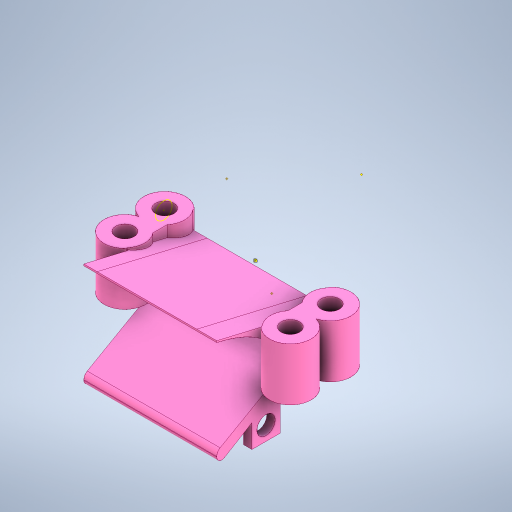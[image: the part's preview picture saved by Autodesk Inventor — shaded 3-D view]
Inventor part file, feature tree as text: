
AUTODESK INVENTOR PART (.ipt)
format: ipt  version: 2024 (Build 280153000, 153)  size: 1,867,264 bytes
history: native  units: mm
features: sketch x24, extrude x19, projected_geometry x11, split x10, other x10, loft x6, boolean_combine x5, plane x4, fillet x2, sweep x2, thicken_offset x2
ambient origin geometry x8: Origin, YZ Plane, XZ Plane, XY Plane, X Axis, Y Axis, Z Axis, Center Point
bodies: Solid1 (feature_tree), Solid2 (feature_tree), Solid19 (feature_tree), Solid20 (feature_tree), Solid21 (feature_tree), Solid22 (feature_tree), Solid23 (feature_tree), Solid3 (feature_tree), Solid4 (feature_tree), Solid5 (feature_tree), Solid6 (feature_tree), Solid7 (feature_tree), Solid8 (feature_tree), Solid9 (feature_tree), Solid10 (feature_tree), Solid11 (feature_tree), Solid12 (feature_tree), Solid13 (feature_tree), Solid14 (feature_tree), Solid15 (feature_tree), Solid16 (feature_tree), Solid17 (feature_tree), Solid18 (feature_tree)
feature tree (95):
  extrude  "Extrusion1"  Depth=3.0mm TaperAngle=0.0deg
  extrude  "Extrusion2"  Depth=3.0mm TaperAngle=0.0deg
  extrude  "Extrusion3"  Depth=40.0mm
  plane  "Work Plane2"
  sketch  "Sketch4"  dims[d4=29.0mm d5=3.0mm d6=0.0mm]
  loft  "Loft1"
  loft  "Loft2"
  loft  "Loft3"
  loft  "Loft4"
  boolean_combine  "Combine1"
  loft  "Loft5"
  fillet  "Fillet1"  [1 undecoded]
  fillet  "Fillet2"  [1 undecoded]
  plane  "Work Plane3"
  extrude  "Extrusion5"  TaperAngle=0.0deg  [1 undecoded]
  extrude  "Extrusion6"  TaperAngle=0.0deg  [1 undecoded]
  extrude  "Extrusion7"  Depth=40.0mm
  extrude  "Extrusion8"  TaperAngle=0.0deg  [1 undecoded]
  extrude  "Extrusion9"  Depth=2.0mm
  extrude  "Extrusion10"  Depth=38.0mm
  extrude  "Extrusion11"  Depth=3.0mm TaperAngle=0.0deg
  extrude  "Extrusion12"  Depth=3.0mm TaperAngle=0.0deg
  extrude  "Extrusion13"  Depth=12.5mm TaperAngle=0.0deg
  extrude  "Extrusion14"  Depth=3.7mm TaperAngle=0.0deg
  extrude  "Extrusion15"  Depth=8.5mm
  split  "Split1"
  split  "Split2"
  split  "Split3"
  split  "Split4"
  split  "Split5"
  split  "Split6"
  split  "Split7"
  boolean_combine  "Combine2"
  split  "Split8"
  boolean_combine  "Combine3"
  boolean_combine  "Combine4"
  extrude  "Extrusion16"  Depth=8.5mm
  extrude  "Extrusion17"  Depth=2.7mm TaperAngle=0.0deg
  sketch  "Sketch36"  dims[d47=15.0mm d48=3.0mm d49=0.0mm]
  sweep  "Sweep1"
  split  "Split9"
  loft  "Loft6"
  thicken_offset  "Thicken1"
  extrude  "Extrusion18"  Depth=10.0mm TaperAngle=0.0deg
  sweep  "Sweep2"
  split  "Split10"
  thicken_offset  "Thicken2"
  boolean_combine  "Combine5"
  plane  "Work Plane4"
  extrude  "Extrusion19"  Depth=10.0mm
  other  "Work Point1"
  other  "Work Point2"
  other  "Work Point3"
  extrude  "Extrusion20"  Depth=10.0mm
  sketch  "Sketch1"  dims[d0=3.0mm d1=0.0mm d2=9.5mm d3=0.0mm]
  plane  "Work Plane1"
  other  "2D Equation Curve1"
  other  "Edges1"
  other  "Edges2"
  other  "Edges3"
  other  "Edges4"
  sketch  "Sketch7"  dims[d7=12.0mm d8=36.0mm d9=40.0mm]
  sketch  "Sketch10"  dims[d10=9.0mm d11=10.0mm]
  sketch  "Sketch12"  dims[d12=3.0mm d13=-6.0mm d14=6.0mm]
  sketch  "Sketch13"  dims[d15=40.0mm d16=26.0mm]
  sketch  "Sketch16"  dims[d17=20.0mm d18=20.0mm]
  projected_geometry  "Projected Loop1"
  sketch  "Sketch18"  dims[d19=0.0mm d20=90.0deg d21=0.0mm d22=90.0deg d23=0.0mm d24=90.0deg d25=0.0mm d26=90.0deg]
  sketch  "Sketch19"  dims[d27=0.0mm d28=90.0deg d29=0.0mm d30=90.0deg]
  projected_geometry  "Projected Loop2"
  projected_geometry  "Projected Loop3"
  projected_geometry  "Projected Loop4"
  projected_geometry  "Projected Loop5"
  sketch  "Sketch23"  dims[d31=0.0mm d32=90.0deg d33=0.0mm d34=90.0deg]
  sketch  "Sketch24"  dims[d35=26.0mm d36=40.0mm]
  sketch  "Sketch28"  dims[d37=4.0mm d38=0.0mm d39=90.0deg]
  sketch  "Sketch29"  dims[d40=0.0mm d41=90.0deg d42=2.0mm]
  sketch  "Sketch35"  dims[d43=1.5mm d46=38.0mm]
  projected_geometry  "Projected Loop11"
  sketch  "3D Sketch2"
  other  "Srf1"
  sketch  "Sketch38"  dims[d50=15.0mm d51=3.0mm d52=0.0mm]
  projected_geometry  "Projected Loop12"
  sketch  "Sketch42"  dims[d53=11.0mm d54=12.5mm d55=0.0mm]
  projected_geometry  "Projected Loop19"
  projected_geometry  "Projected Loop20"
  sketch  "Sketch43"  dims[d56=11.0mm d57=3.7mm d58=0.0mm]
  sketch  "Sketch46"  dims[d59=20.0mm d60=0.0mm d61=8.5mm]
  projected_geometry  "Projected Loop21"
  sketch  "3D Sketch3"
  sketch  "Sketch47"  dims[d62=8.5mm d63=8.5mm]
  projected_geometry  "Projected Loop22"
  sketch  "Sketch49"  dims[d64=8.5mm d65=2.7mm d66=0.0mm]
  sketch  "Sketch50"  dims[d67=40.0mm d68=10.0mm d69=2.7mm d70=0.0mm d71=2.5mm d72=0.0mm d73=2.5mm d74=0.0mm d75=9.0mm d76=2.0mm d77=0.0mm d78=0.0mm d79=7.0mm d80=5.5mm d81=8.5mm d82=8.5mm d83=2.5mm d84=0.0mm d85=2.5mm d86=0.0mm d87=0.5mm d88=0.0mm d89=0.0mm d91=10.0mm d92=10.0mm d93=0.1mm d94=0.0mm d95=16.0mm d96=2.5mm d97=4.0mm d98=2.5mm d99=2.5mm d100=5.0mm d101=5.0mm d102=2.5mm d103=2.5mm d104=2.5mm d105=2.5mm d106=0.0mm d107=0.0mm d108=2.5mm d109=2.5mm d110=0.0mm d111=90.0deg d112=0.0mm d113=90.0deg d114=0.1mm d115=0.1mm d116=0.1mm d117=0.0mm d118=15.0mm d119=3.0mm d120=1.6mm d121=1.5mm d122=16.5mm d125=5.5mm d126=2.5mm d127=2.5mm d128=0.0mm d129=0.0mm d130=0.1mm d131=0.1mm d132=58.25mm d133=6.0mm d134=16.0mm d135=0.0mm d136=12.0mm d137=12.0mm d138=12.0mm d139=12.0mm d140=10.0mm d141=0.0mm]
  other  "Unwrap1"
note: 5 required parameter values undecoded (feature->parameter linkage not recoverable at this tier; creation-order binding heuristic only, values carry confidence <= 0.55)
